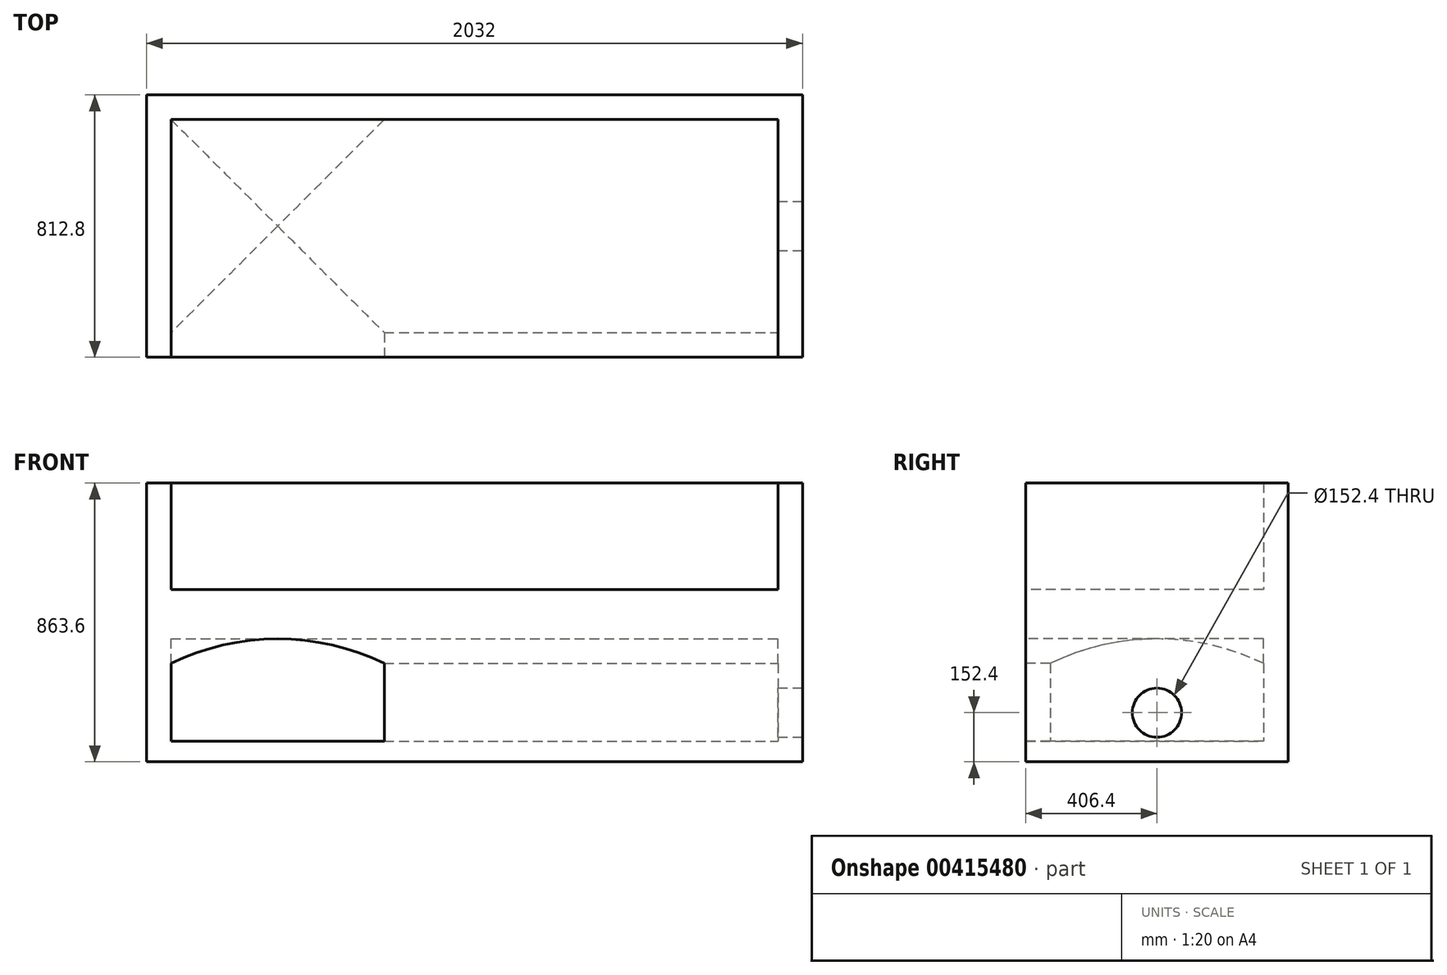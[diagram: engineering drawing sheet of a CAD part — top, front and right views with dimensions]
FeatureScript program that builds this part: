
annotation { "Feature Type Name" : "Feature", "Feature Type Description" : "" }
export const myFeature = defineFeature(function(context is Context, id is Id, definition is map)
    precondition{}
    {
        {
            var Q0;
            Q0=qCreatedBy(makeId("Top.planeOp"),FACE);
            var sketch = newSketch(context, id + "F0", { "sketchPlane" : qUnion([Q0])});
            skLineSegment(sketch, "E0.bottom", {"start": v(1016, -406.4) * mm, "end": v(-1016, -406.4) * mm});
            skLineSegment(sketch, "E0.top", {"start": v(1016, 406.4) * mm, "end": v(-1016, 406.4) * mm});
            skLineSegment(sketch, "E0.left", {"start": v(1016, -406.4) * mm, "end": v(1016, 406.4) * mm});
            skLineSegment(sketch, "E0.right", {"start": v(-1016, -406.4) * mm, "end": v(-1016, 406.4) * mm});
            skPoint(sketch, "E0.middle", {"position": v(0, 0) * mm});
            skSolve(sketch);
        }
        {
            var Q0;
            Q0=makeQuery(id+"F0.imprint","IMPRINT",FACE,{"disambiguationData":[TD([[makeQuery(id+"F0.imprint","IMPRINT",EDGE,{"derivedFrom":sQuery(id+"F0.wireOp",EDGE,"E0.bottom")}),-1.0]])]});
            extrude(context, id + "F1", {"entities" : qUnion([Q0]), "depth" : 914.4 * mm});
        }
        {
            var Q0;
            Q0=makeQuery(id+"F1.opExtrude","SWEPT_FACE",FACE,{"disambiguationData":[OSD([sQuery(id+"F0.wireOp",EDGE,"E0.left")])]});
            var sketch = newSketch(context, id + "F2", { "sketchPlane" : qUnion([Q0])});
            skLineSegment(sketch, "E1", {"start": v(-406.4, 457.2) * mm, "end": v(406.4, 457.2) * mm});
            skPoint(sketch, "E2", {"position": v(0, 457.2) * mm});
            skPoint(sketch, "E3", {"position": v(0, 381) * mm});
            skPoint(sketch, "E4", {"position": v(-406.4, 304.8) * mm});
            skPoint(sketch, "E5", {"position": v(406.4, 304.8) * mm});
            skPoint(sketch, "E6", {"position": v(-330.2, 304.8) * mm});
            skPoint(sketch, "E7", {"position": v(330.2, 304.8) * mm});
            skArc(sketch, "E8", {"start": v(330.2, 304.8) * mm, "mid": v(0, 381) * mm, "end": v(-330.2, 304.8) * mm});
            skLineSegment(sketch, "E9", {"start": v(-330.2, 304.8) * mm, "end": v(-330.2, 63.5) * mm});
            skLineSegment(sketch, "E10", {"start": v(-330.2, 63.5) * mm, "end": v(330.2, 63.5) * mm});
            skLineSegment(sketch, "E11", {"start": v(330.2, 63.5) * mm, "end": v(330.2, 304.8) * mm});
            skSolve(sketch);
        }
        {
            var Q0;
            Q0=makeQuery(id+"F1.opExtrude","SWEPT_FACE",FACE,{"disambiguationData":[OSD([sQuery(id+"F0.wireOp",EDGE,"E0.bottom")])]});
            var sketch = newSketch(context, id + "F3", { "sketchPlane" : qUnion([Q0])});
            skLineSegment(sketch, "E12", {"start": v(1016, 457.2) * mm, "end": v(-1016, 457.2) * mm});
            skLineSegment(sketch, "E13.bottom", {"start": v(-939.8, 863.6) * mm, "end": v(939.8, 863.6) * mm});
            skLineSegment(sketch, "E13.top", {"start": v(-939.8, 533.4) * mm, "end": v(939.8, 533.4) * mm});
            skLineSegment(sketch, "E13.left", {"start": v(-939.8, 863.6) * mm, "end": v(-939.8, 533.4) * mm});
            skLineSegment(sketch, "E13.right", {"start": v(939.8, 863.6) * mm, "end": v(939.8, 533.4) * mm});
            skSolve(sketch);
        }
        {
            var Q0;
            Q0=makeQuery(id+"F2.imprint","IMPRINT",FACE,{"disambiguationData":[TD([[makeQuery(id+"F2.imprint","IMPRINT",EDGE,{"derivedFrom":sQuery(id+"F2.wireOp",EDGE,"E8")}),1.0]])]});
            extrude(context, id + "F4", {"entities" : qUnion([Q0]), "operationType" : NewBodyOperationType.REMOVE, "oppositeDirection" : true, "depth" : 1955.8 * mm});
        }
        {
            var Q0;
            Q0=makeQuery(id+"F3.imprint","IMPRINT",FACE,{"disambiguationData":[TD([[makeQuery(id+"F3.imprint","IMPRINT",EDGE,{"derivedFrom":sQuery(id+"F3.wireOp",EDGE,"E13.bottom")}),-1.0]])]});
            extrude(context, id + "F5", {"entities" : qUnion([Q0]), "operationType" : NewBodyOperationType.REMOVE, "oppositeDirection" : true, "depth" : 736.6 * mm});
        }
        {
            var Q0;
            Q0=makeQuery(id+"F1.opExtrude","SWEPT_FACE",FACE,{"disambiguationData":[OSD([sQuery(id+"F0.wireOp",EDGE,"E0.bottom")])]});
            var sketch = newSketch(context, id + "F6", { "sketchPlane" : qUnion([Q0])});
            skLineSegment(sketch, "E14.bottom", {"start": v(-939.8, 63.5) * mm, "end": v(-279.4, 63.5) * mm});
            skLineSegment(sketch, "E14.top", {"start": v(-939.8, 304.8) * mm, "end": v(-279.4, 304.8) * mm});
            skLineSegment(sketch, "E14.left", {"start": v(-939.8, 63.5) * mm, "end": v(-939.8, 304.8) * mm});
            skLineSegment(sketch, "E14.right", {"start": v(-279.4, 63.5) * mm, "end": v(-279.4, 304.8) * mm});
            skLineSegment(sketch, "E15", {"start": v(1016, 457.2) * mm, "end": v(-1016, 457.2) * mm});
            skPoint(sketch, "E16", {"position": v(-609.6, 304.8) * mm});
            skArc(sketch, "E17", {"start": v(-279.4, 304.8) * mm, "mid": v(-609.6, 381) * mm, "end": v(-939.8, 304.8) * mm});
            skPoint(sketch, "E18", {"position": v(-609.6, 381) * mm});
            skSolve(sketch);
        }
        {
            var Q0;
            Q0=makeQuery(id+"F6.imprint","IMPRINT",FACE,{"disambiguationData":[TD([[makeQuery(id+"F6.imprint","IMPRINT",EDGE,{"derivedFrom":sQuery(id+"F6.wireOp",EDGE,"E14.bottom")}),1.0]])]});
            var Q1;
            Q1=makeQuery(id+"F6.imprint","IMPRINT",FACE,{"disambiguationData":[TD([[makeQuery(id+"F6.imprint","IMPRINT",EDGE,{"derivedFrom":sQuery(id+"F6.wireOp",EDGE,"E14.top")}),1.0]])]});
            extrude(context, id + "F7", {"entities" : qUnion([Q0, Q1]), "operationType" : NewBodyOperationType.REMOVE, "oppositeDirection" : true, "depth" : 736.6 * mm});
        }
        {
            var Q0;
            Q0=makeQuery(id+"F7.boolean.opBoolean","MERGE",FACE,{"derivedFrom":[makeQuery(id+"F4.boolean.opBoolean","COPY",FACE,{"derivedFrom":makeQuery(id+"F4.opExtrude","SWEPT_FACE",FACE,{"disambiguationData":[OSD([sQuery(id+"F2.wireOp",EDGE,"E10")])]})}),makeQuery(id+"F7.opExtrude","SWEPT_FACE",FACE,{"disambiguationData":[OSD([sQuery(id+"F6.wireOp",EDGE,"E14.bottom")])]})]});
            var sketch = newSketch(context, id + "F8", { "sketchPlane" : qUnion([Q0])});
            skLineSegment(sketch, "E19", {"start": v(939.8, 330.2) * mm, "end": v(939.8, -330.2) * mm});
            skSolve(sketch);
        }
        {
            var Q0;
            {var subQ0=sQuery(id+"F8.wireOp",EDGE,"E19");Q0=makeQuery(id+"F8.imprint","IMPRINT",FACE,{"disambiguationData":[TD([[makeQuery(id+"F8.imprint","IMPRINT",EDGE,{"derivedFrom":subQ0}),1.0]])]});}
            extrude(context, id + "F9", {"entities" : qUnion([Q0]), "operationType" : NewBodyOperationType.ADD, "endBound" : BoundingType.UP_TO_NEXT, "depth" : 25.4 * mm});
        }
        {
            var Q0;
            Q0=makeQuery(id+"F9.boolean.opBoolean","MERGE",FACE,{"derivedFrom":[makeQuery(id+"F1.opExtrude","SWEPT_FACE",FACE,{"disambiguationData":[OSD([sQuery(id+"F0.wireOp",EDGE,"E0.left")])]}),makeQuery(id+"F9.opExtrude","SWEPT_FACE",FACE,{"disambiguationData":[OSD([sQuery(id+"F2.wireOp",EDGE,"E10")])]})]});
            var sketch = newSketch(context, id + "F10", { "sketchPlane" : qUnion([Q0])});
            skCircle(sketch, "E20", {"center": v(0, 152.4) * mm, "radius": 76.2 * mm});
            skPoint(sketch, "E20.centerSnap0", {"position": v(0, 0) * mm});
            skSolve(sketch);
        }
        {
            var Q0;
            Q0=makeQuery(id+"F10.imprint","IMPRINT",FACE,{"disambiguationData":[TD([[makeQuery(id+"F10.imprint","IMPRINT",EDGE,{"derivedFrom":sQuery(id+"F10.wireOp",EDGE,"E20")}),1.0]])]});
            extrude(context, id + "F11", {"entities" : qUnion([Q0]), "operationType" : NewBodyOperationType.REMOVE, "endBound" : BoundingType.UP_TO_NEXT, "oppositeDirection" : true, "depth" : 25.4 * mm});
        }
        {
            var Q0;
            Q0=makeQuery(id+"F1.opExtrude","CAP_FACE",FACE,{"disambiguationData":[OSD([sQuery(id+"F0.wireOp",EDGE,"E0.bottom"),sQuery(id+"F0.wireOp",EDGE,"E0.top"),sQuery(id+"F0.wireOp",EDGE,"E0.left"),sQuery(id+"F0.wireOp",EDGE,"E0.right")])],"isStart":false});
            extrude(context, id + "F12", {"entities" : qUnion([Q0]), "operationType" : NewBodyOperationType.REMOVE, "oppositeDirection" : true, "depth" : 50.8 * mm});
        }
    });
